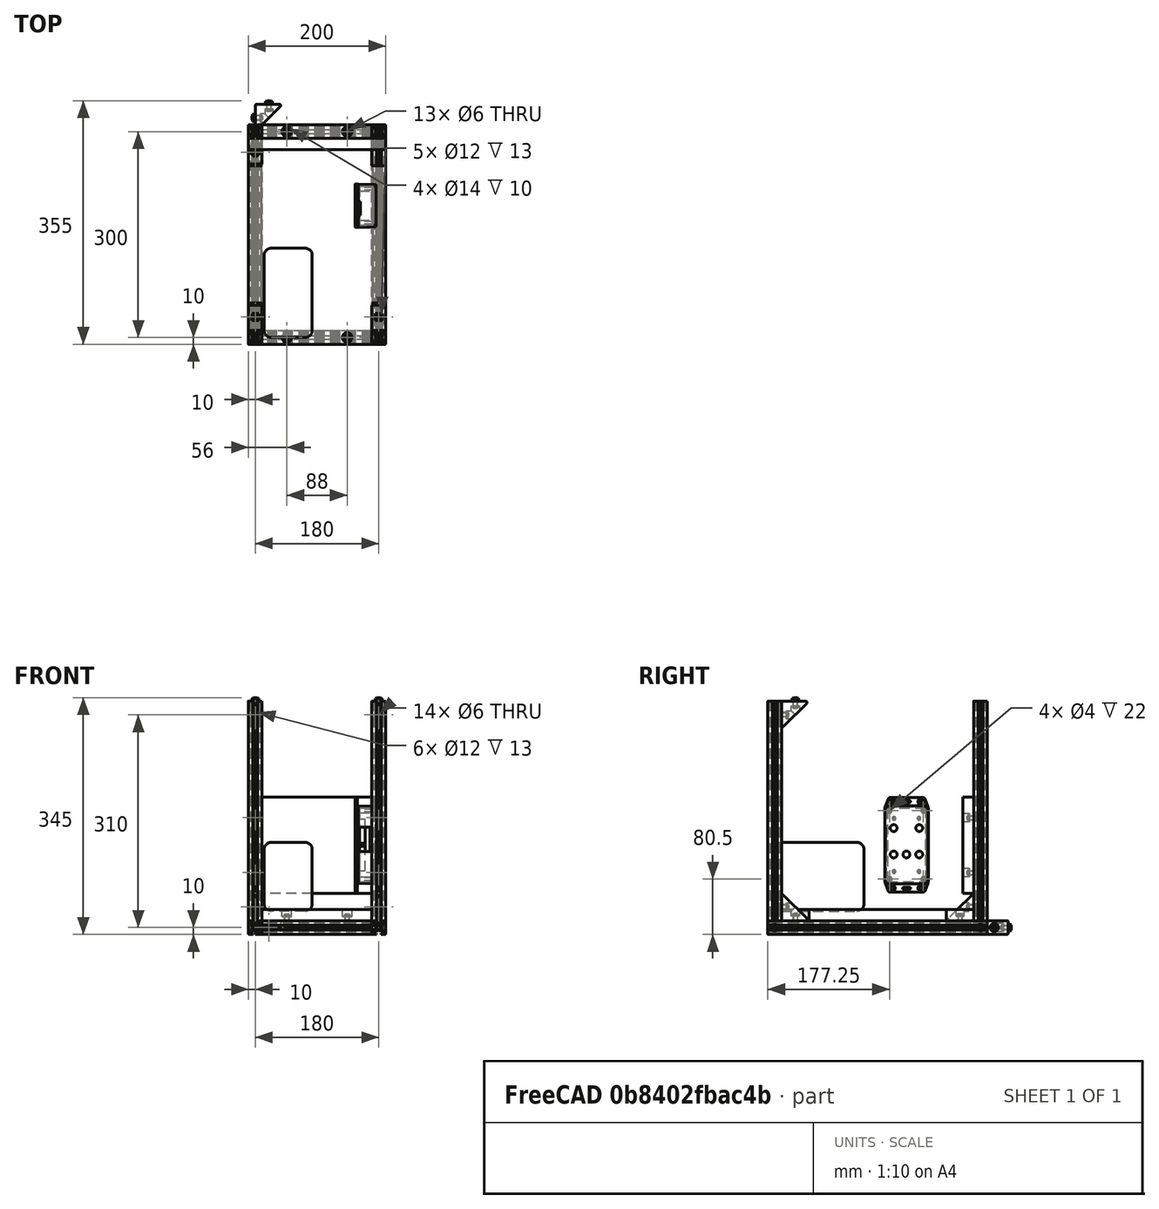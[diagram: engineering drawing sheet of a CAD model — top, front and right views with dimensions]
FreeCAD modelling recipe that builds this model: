
FCSTD DOCUMENT  (FreeCAD 0.17R9796 (Git))
Label: UPKframeNG2c
License: All rights reserved
LicenseURL: http://en.wikipedia.org/wiki/All_rights_reserved
objects: Part::Feature×55, Part::FeaturePython×20, Part::Compound×11, App::Part×6, Part::Cylinder×5, App::FeaturePython×4, Part::Box×4, Part::Cut×4, PartDesign::Body×1, PartDesign::Pocket×1, Part::Fillet×1, Part::MultiFuse×1
note: 104 computed .brp shape members not serialized (recipe doc carries the construction recipe); baked Part::Feature solids carry a one-line shape summary decoded from their .brp

FEATURE [Part::Feature] Pocket003001  label="tslot32con"
  Placement = pos=(0,10,10) rot=(1,0,0;1.5708rad)
  shape: bbox 20 x 320 x 20 mm, 150 faces (baked)
FEATURE [Part::Feature] Pocket003002  label="tslot16"
  Placement = pos=(10,0,10) rot=(0,1,0;1.5708rad)
  shape: bbox 160 x 20 x 20 mm, 94 faces (baked)
FEATURE [Part::Feature] Pocket003006  label="tslot16_001"
  Placement = pos=(10,-300,10) rot=(0,1,0;1.5708rad)
  shape: bbox 160 x 20 x 20 mm, 94 faces (baked)
FEATURE [Part::Feature] Pocket003007  label="tslot32con_001"
  Placement = pos=(180,-310,10) rot=(0,0.707107,0.707107;3.14159rad)
  shape: bbox 20 x 320 x 20 mm, 150 faces (baked)
FEATURE [Part::FeaturePython] Screw  label="M6x25-Screw"  # Fasteners workbench fastener (typed FeaturePython)
  Placement = pos=(-4,0,10) rot=(0,-1,0;1.5708rad)
  diameter = 7
  invert = false
  length = 6
  matchOuter = false
  offset = 0
  thread = false
  type = 15
FEATURE [Part::FeaturePython] Screw001  label="M6x25-Screw004"  # Fasteners workbench fastener (typed FeaturePython)
  Placement = pos=(-4,-300,10) rot=(0,-1,0;1.5708rad)
  diameter = 7
  invert = false
  length = 6
  matchOuter = false
  offset = 0
  thread = false
  type = 15
FEATURE [Part::FeaturePython] Screw002  label="M6x25-Screw005"  # Fasteners workbench fastener (typed FeaturePython)
  Placement = pos=(184,0,10) rot=(0,1,0;1.5708rad)
  diameter = 7
  invert = false
  length = 6
  matchOuter = false
  offset = 0
  thread = false
  type = 15
FEATURE [Part::FeaturePython] Screw004  label="M6x25-Screw006"  # Fasteners workbench fastener (typed FeaturePython)
  Placement = pos=(184,-300,10) rot=(0,1,0;1.5708rad)
  diameter = 7
  invert = false
  length = 6
  matchOuter = false
  offset = 0
  thread = false
  type = 15
FEATURE [App::Part] Part  label="lower_frame"
  Group = -> [Pocket003001,Pocket003002,Pocket003006,Pocket003007,Screw,Screw001,Screw002,Screw004]
  License = CC BY 3.0
  LicenseURL = http://creativecommons.org/licenses/by/3.0/
  Origin = -> PartOrigin
FEATURE [Part::Feature] Pocket003008  label="tslot32con001"
  Placement = pos=(0,10,10) rot=(1,0,0;1.5708rad)
  shape: bbox 20 x 320 x 20 mm, 150 faces (baked)
FEATURE [Part::Feature] Pocket003009  label="tslot041"
  Placement = pos=(10,0,10) rot=(0,1,0;1.5708rad)
  shape: bbox 160 x 20 x 20 mm, 94 faces (baked)
FEATURE [Part::Feature] Pocket003010  label="tslot16_002"
  Placement = pos=(10,-300,10) rot=(0,1,0;1.5708rad)
  shape: bbox 160 x 20 x 20 mm, 94 faces (baked)
FEATURE [Part::Feature] Pocket003011  label="tslot32con_002"
  Placement = pos=(180,-310,10) rot=(0,0.707107,0.707107;3.14159rad)
  shape: bbox 20 x 320 x 20 mm, 150 faces (baked)
FEATURE [Part::FeaturePython] Screw005  label="M6x25-Screw007"  # Fasteners workbench fastener (typed FeaturePython)
  Placement = pos=(-4,0,10) rot=(0,-1,0;1.5708rad)
  diameter = 7
  invert = false
  length = 6
  matchOuter = false
  offset = 0
  thread = false
  type = 15
FEATURE [Part::FeaturePython] Screw006  label="M6x25-Screw008"  # Fasteners workbench fastener (typed FeaturePython)
  Placement = pos=(-4,-300,10) rot=(0,-1,0;1.5708rad)
  diameter = 7
  invert = false
  length = 6
  matchOuter = false
  offset = 0
  thread = false
  type = 15
FEATURE [Part::FeaturePython] Screw007  label="M6x25-Screw009"  # Fasteners workbench fastener (typed FeaturePython)
  Placement = pos=(184,0,10) rot=(0,1,0;1.5708rad)
  diameter = 7
  invert = false
  length = 6
  matchOuter = false
  offset = 0
  thread = false
  type = 15
FEATURE [Part::FeaturePython] Screw008  label="M6x25-Screw010"  # Fasteners workbench fastener (typed FeaturePython)
  Placement = pos=(184,-300,10) rot=(0,1,0;1.5708rad)
  diameter = 7
  invert = false
  length = 6
  matchOuter = false
  offset = 0
  thread = false
  type = 15
FEATURE [App::Part] Part001  label="upper_frame"
  Group = -> [Pocket003008,Pocket003009,Pocket003010,Pocket003011,Screw005,Screw006,Screw007,Screw008]
  License = CC BY 3.0
  LicenseURL = http://creativecommons.org/licenses/by/3.0/
  Origin = -> PartOrigin001
  Placement = pos=(0,0,340) rot=(0,0,1;0rad)
FEATURE [Part::Feature] Fillet004001  label="Fillet005"
  shape: bbox 37.5 x 37.5 x 20 mm, 26 faces (baked)
FEATURE [Part::FeaturePython] Screw009  label="M6x12-Screw"  # Fasteners workbench fastener (typed FeaturePython)
  Placement = pos=(7,20,10) rot=(0,1,0;1.5708rad)
  diameter = 4
  invert = false
  length = 1
  matchOuter = false
  offset = 0
  thread = false
  type = 20
FEATURE [Part::Feature] Body001  label="m6nutplate"
  Placement = pos=(-1.5,15,5) rot=(0,-1,0;1.5708rad)
  shape: bbox 3 x 10 x 10 mm, 9 faces (baked)
FEATURE [App::Part] Part002  label="cornerstonescrewnut"
  License = CC BY 3.0
  LicenseURL = http://creativecommons.org/licenses/by/3.0/
  Origin = -> PartOrigin002
  Placement = pos=(10,-50,20) rot=(0,-1,0;1.5708rad)
FEATURE [Part::FeaturePython] Screw010  label="M6x12-Screw001"  # Fasteners workbench fastener (typed FeaturePython)
  Placement = pos=(20,33,10) rot=(1,0,0;1.5708rad)
  diameter = 4
  invert = false
  length = 1
  matchOuter = false
  offset = 0
  thread = false
  type = 20
FEATURE [Part::Feature] Body002  label="m6nutplate001"
  Placement = pos=(15,41.5,5) rot=(0.57735,0.57735,0.57735;4.18879rad)
  shape: bbox 10 x 3 x 10 mm, 9 faces (baked)
FEATURE [Part::Feature] Fillet004002  label="Fillet006"
  shape: bbox 37.5 x 37.5 x 20 mm, 26 faces (baked)
FEATURE [Part::FeaturePython] Screw011  label="M6x12-Screw002"  # Fasteners workbench fastener (typed FeaturePython)
  Placement = pos=(7,20,10) rot=(0,1,0;1.5708rad)
  diameter = 4
  invert = false
  length = 1
  matchOuter = false
  offset = 0
  thread = false
  type = 20
FEATURE [Part::Feature] Body003  label="m6nutplate002"
  Placement = pos=(-1.5,15,5) rot=(0,-1,0;1.5708rad)
  shape: bbox 3 x 10 x 10 mm, 9 faces (baked)
FEATURE [Part::FeaturePython] Screw012  label="M6x12-Screw003"  # Fasteners workbench fastener (typed FeaturePython)
  Placement = pos=(20,33,10) rot=(1,0,0;1.5708rad)
  diameter = 4
  invert = false
  length = 1
  matchOuter = false
  offset = 0
  thread = false
  type = 20
FEATURE [Part::Feature] Body004  label="m6nutplate003"
  Placement = pos=(15,41.5,5) rot=(0.57735,0.57735,0.57735;4.18879rad)
  shape: bbox 10 x 3 x 10 mm, 9 faces (baked)
FEATURE [App::Part] Part003  label="cornerstonescrewnut001"
  Group = -> [Body003,Screw011,Fillet004002,Screw012,Body004,PartOrigin002,Body001,Screw009,Fillet004001,Screw010,Body002,Part002]
  License = CC BY 3.0
  LicenseURL = http://creativecommons.org/licenses/by/3.0/
  Origin = -> PartOrigin003
  Placement = pos=(190,-50,20) rot=(0,-1,0;1.5708rad)
FEATURE [Part::Feature] Fillet004003  label="Fillet007"
  shape: bbox 37.5 x 37.5 x 20 mm, 26 faces (baked)
FEATURE [Part::FeaturePython] Screw013  label="M6x12-Screw004"  # Fasteners workbench fastener (typed FeaturePython)
  Placement = pos=(7,20,10) rot=(0,1,0;1.5708rad)
  diameter = 4
  invert = false
  length = 1
  matchOuter = false
  offset = 0
  thread = false
  type = 20
FEATURE [Part::Feature] Body005  label="m6nutplate004"
  Placement = pos=(-1.5,15,5) rot=(0,-1,0;1.5708rad)
  shape: bbox 3 x 10 x 10 mm, 9 faces (baked)
FEATURE [Part::FeaturePython] Screw014  label="M6x12-Screw005"  # Fasteners workbench fastener (typed FeaturePython)
  Placement = pos=(20,33,10) rot=(1,0,0;1.5708rad)
  diameter = 4
  invert = false
  length = 1
  matchOuter = false
  offset = 0
  thread = false
  type = 20
FEATURE [Part::Feature] Body006  label="m6nutplate005"
  Placement = pos=(15,41.5,5) rot=(0.57735,0.57735,0.57735;4.18879rad)
  shape: bbox 10 x 3 x 10 mm, 9 faces (baked)
FEATURE [App::Part] Part004  label="cornerstonescrewnut002"
  Group = -> [Body005,Screw013,Fillet004003,Screw014,Body006]
  License = CC BY 3.0
  LicenseURL = http://creativecommons.org/licenses/by/3.0/
  Origin = -> PartOrigin004
  Placement = pos=(-10,-50,340) rot=(0,1,0;1.5708rad)
FEATURE [Part::Feature] Fillet004004  label="Fillet008"
  shape: bbox 37.5 x 37.5 x 20 mm, 26 faces (baked)
FEATURE [Part::FeaturePython] Screw015  label="M6x12-Screw006"  # Fasteners workbench fastener (typed FeaturePython)
  Placement = pos=(7,20,10) rot=(0,1,0;1.5708rad)
  diameter = 4
  invert = false
  length = 1
  matchOuter = false
  offset = 0
  thread = false
  type = 20
FEATURE [Part::Feature] Body007  label="m6nutplate006"
  Placement = pos=(-1.5,15,5) rot=(0,-1,0;1.5708rad)
  shape: bbox 3 x 10 x 10 mm, 9 faces (baked)
FEATURE [Part::FeaturePython] Screw016  label="M6x12-Screw007"  # Fasteners workbench fastener (typed FeaturePython)
  Placement = pos=(20,33,10) rot=(1,0,0;1.5708rad)
  diameter = 4
  invert = false
  length = 1
  matchOuter = false
  offset = 0
  thread = false
  type = 20
FEATURE [Part::Feature] Body008  label="m6nutplate007"
  Placement = pos=(15,41.5,5) rot=(0.57735,0.57735,0.57735;4.18879rad)
  shape: bbox 10 x 3 x 10 mm, 9 faces (baked)
FEATURE [App::Part] Part005  label="cornerstonescrewnut003"
  Group = -> [Body007,Screw015,Fillet004004,Screw016,Body008]
  License = CC BY 3.0
  LicenseURL = http://creativecommons.org/licenses/by/3.0/
  Origin = -> PartOrigin005
  Placement = pos=(170,-50,340) rot=(0,1,0;1.5708rad)
FEATURE [Part::Feature] Body009001  label="m6nutplate010"
  Placement = pos=(-1.5,15,5) rot=(0,-1,0;1.5708rad)
  shape: bbox 3 x 10 x 10 mm, 9 faces (baked)
FEATURE [Part::Feature] Body010001  label="m6nutplate011"
  Placement = pos=(15,41.5,5) rot=(0.57735,0.57735,0.57735;4.18879rad)
  shape: bbox 10 x 3 x 10 mm, 9 faces (baked)
FEATURE [Part::Feature] Screw018001  label="M6x12-Screw010"
  Placement = pos=(20,33,10) rot=(1,0,0;1.5708rad)
  shape: bbox 10.5 x 15.3 x 10.5 mm, 15 faces (baked)
FEATURE [Part::Feature] Screw017001  label="M6x12-Screw011"
  Placement = pos=(7,20,10) rot=(0,1,0;1.5708rad)
  shape: bbox 15.3 x 10.5 x 10.5 mm, 15 faces (baked)
FEATURE [Part::Feature] Fillet004005001  label="Fillet010"
  shape: bbox 37.5 x 37.5 x 20 mm, 26 faces (baked)
FEATURE [Part::Compound] Compound
  Links = -> [Body009001,Fillet004005001,Screw017001,Body010001,Screw018001]
  Placement = pos=(10,-250,340) rot=(0.707107,0,-0.707107;3.14159rad)
FEATURE [Part::Feature] Body010002  label="m6nutplate012"
  Placement = pos=(-1.5,15,5) rot=(0,-1,0;1.5708rad)
  shape: bbox 3 x 10 x 10 mm, 9 faces (baked)
FEATURE [Part::Feature] Body010003  label="m6nutplate013"
  Placement = pos=(15,41.5,5) rot=(0.57735,0.57735,0.57735;4.18879rad)
  shape: bbox 10 x 3 x 10 mm, 9 faces (baked)
FEATURE [Part::Feature] Screw018002  label="M6x12-Screw012"
  Placement = pos=(20,33,10) rot=(1,0,0;1.5708rad)
  shape: bbox 10.5 x 15.3 x 10.5 mm, 15 faces (baked)
FEATURE [Part::Feature] Screw018003  label="M6x12-Screw013"
  Placement = pos=(7,20,10) rot=(0,1,0;1.5708rad)
  shape: bbox 15.3 x 10.5 x 10.5 mm, 15 faces (baked)
FEATURE [Part::Feature] Fillet004005002  label="Fillet011"
  shape: bbox 37.5 x 37.5 x 20 mm, 26 faces (baked)
FEATURE [Part::Compound] Compound001
  Links = -> [Body010002,Fillet004005002,Screw018003,Body010003,Screw018002]
  Placement = pos=(190,-250,340) rot=(0.707107,0,-0.707107;3.14159rad)
FEATURE [Part::Feature] Body010004  label="m6nutplate014"
  Placement = pos=(-1.5,15,5) rot=(0,-1,0;1.5708rad)
  shape: bbox 3 x 10 x 10 mm, 9 faces (baked)
FEATURE [Part::Feature] Body010005  label="m6nutplate015"
  Placement = pos=(15,41.5,5) rot=(0.57735,0.57735,0.57735;4.18879rad)
  shape: bbox 10 x 3 x 10 mm, 9 faces (baked)
FEATURE [Part::Feature] Screw018004  label="M6x12-Screw014"
  Placement = pos=(20,33,10) rot=(1,0,0;1.5708rad)
  shape: bbox 10.5 x 15.3 x 10.5 mm, 15 faces (baked)
FEATURE [Part::Feature] Screw018005  label="M6x12-Screw015"
  Placement = pos=(7,20,10) rot=(0,1,0;1.5708rad)
  shape: bbox 15.3 x 10.5 x 10.5 mm, 15 faces (baked)
FEATURE [Part::Feature] Fillet004005003  label="Fillet012"
  shape: bbox 37.5 x 37.5 x 20 mm, 26 faces (baked)
FEATURE [Part::Compound] Compound002
  Links = -> [Body010004,Fillet004005003,Screw018005,Body010005,Screw018004]
  Placement = pos=(10,-290,60) rot=(0.57735,0.57735,-0.57735;4.18879rad)
FEATURE [Part::Feature] Body010006  label="m6nutplate016"
  Placement = pos=(-1.5,15,5) rot=(0,-1,0;1.5708rad)
  shape: bbox 3 x 10 x 10 mm, 9 faces (baked)
FEATURE [Part::Feature] Body010007  label="m6nutplate017"
  Placement = pos=(15,41.5,5) rot=(0.57735,0.57735,0.57735;4.18879rad)
  shape: bbox 10 x 3 x 10 mm, 9 faces (baked)
FEATURE [Part::Feature] Screw018006  label="M6x12-Screw016"
  Placement = pos=(20,33,10) rot=(1,0,0;1.5708rad)
  shape: bbox 10.5 x 15.3 x 10.5 mm, 15 faces (baked)
FEATURE [Part::Feature] Screw018007  label="M6x12-Screw017"
  Placement = pos=(7,20,10) rot=(0,1,0;1.5708rad)
  shape: bbox 15.3 x 10.5 x 10.5 mm, 15 faces (baked)
FEATURE [Part::Feature] Fillet004005004  label="Fillet013"
  shape: bbox 37.5 x 37.5 x 20 mm, 26 faces (baked)
FEATURE [Part::Compound] Compound003
  Links = -> [Body010006,Fillet004005004,Screw018007,Body010007,Screw018006]
  Placement = pos=(190,-290,60) rot=(0.57735,0.57735,-0.57735;4.18879rad)
FEATURE [Part::Feature] Pocket001001  label="tslot32"
  Placement = pos=(0,0,20) rot=(0,0,1;0rad)
  shape: bbox 20 x 20 x 320 mm, 94 faces (baked)
FEATURE [Part::Feature] Body010008  label="m6nutplate018"
  Placement = pos=(-1.5,15,5) rot=(0,-1,0;1.5708rad)
  shape: bbox 3 x 10 x 10 mm, 9 faces (baked)
FEATURE [Part::Feature] Body010009  label="m6nutplate019"
  Placement = pos=(15,41.5,5) rot=(0.57735,0.57735,0.57735;4.18879rad)
  shape: bbox 10 x 3 x 10 mm, 9 faces (baked)
FEATURE [Part::Feature] Screw018008  label="M6x12-Screw018"
  Placement = pos=(20,33,10) rot=(1,0,0;1.5708rad)
  shape: bbox 10.5 x 15.3 x 10.5 mm, 15 faces (baked)
FEATURE [Part::Feature] Screw018009  label="M6x12-Screw019"
  Placement = pos=(7,20,10) rot=(0,1,0;1.5708rad)
  shape: bbox 15.3 x 10.5 x 10.5 mm, 15 faces (baked)
FEATURE [Part::Feature] Fillet004005005  label="Fillet014"
  shape: bbox 37.5 x 37.5 x 20 mm, 26 faces (baked)
FEATURE [Part::Compound] Compound004
  Links = -> [Body010008,Fillet004005005,Screw018009,Body010009,Screw018008]
  Placement = pos=(-10,-10,60) rot=(0.57735,-0.57735,0.57735;4.18879rad)
FEATURE [Part::Feature] Pocket003012  label="tslot32_001"
  Placement = pos=(0,-300,20) rot=(0,0,1;0rad)
  shape: bbox 20 x 20 x 320 mm, 94 faces (baked)
FEATURE [Part::Feature] Pocket003013  label="tslot32_002"
  Placement = pos=(180,0,20) rot=(0,0,1;0rad)
  shape: bbox 20 x 20 x 320 mm, 94 faces (baked)
FEATURE [Part::Feature] Pocket003014  label="tslot32_003"
  Placement = pos=(180,-300,20) rot=(0,0,1;0rad)
  shape: bbox 20 x 20 x 320 mm, 94 faces (baked)
FEATURE [PartDesign::Body] Body010027
FEATURE [Part::FeaturePython] Screw018021  label="M6x12-Screw032"  # Fasteners workbench fastener (typed FeaturePython)
  diameter = 4
  invert = false
  length = 1
  matchOuter = false
  offset = 0
  thread = false
  type = 20
FEATURE [Part::Feature] Body010028  label="m6nutplate032"
  Placement = pos=(5,-5,-8.39) rot=(0,1,0;3.14159rad)
  shape: bbox 10 x 10 x 3 mm, 9 faces (baked)
FEATURE [App::FeaturePython] circularEdgeConstraint009  # a2plus constraint (typed FeaturePython)
  Object1 = Screw
  Object2 = Body001
  SubElement1 = Edge7
  SubElement2 = Edge20
  Type = circularEdge
  directionConstraint = 1
  lockRotation = false
  offset = 0
FEATURE [Part::Compound] Compound017  label="nutplate12screw008"
  Links = -> [Screw018021,circularEdgeConstraint009,Body010028]
  Placement = pos=(10,30,6) rot=(0,0,1;0rad)
FEATURE [Part::FeaturePython] Screw018022  label="M6x12-Screw033"  # Fasteners workbench fastener (typed FeaturePython)
  diameter = 4
  invert = false
  length = 1
  matchOuter = false
  offset = 0
  thread = false
  type = 20
FEATURE [Part::Feature] Body010029  label="m6nutplate033"
  Placement = pos=(5,-5,-8.39) rot=(0,1,0;3.14159rad)
  shape: bbox 10 x 10 x 3 mm, 9 faces (baked)
FEATURE [App::FeaturePython] circularEdgeConstraint010  # a2plus constraint (typed FeaturePython)
  Object1 = Screw
  Object2 = Body001
  SubElement1 = Edge7
  SubElement2 = Edge20
  Type = circularEdge
  directionConstraint = 1
  lockRotation = false
  offset = 0
FEATURE [Part::Compound] Compound018  label="nutplate12screw009"
  Links = -> [Screw018022,circularEdgeConstraint010,Body010029]
  Placement = pos=(10,110,6) rot=(0,0,1;0rad)
FEATURE [Part::FeaturePython] Screw018023  label="M6x12-Screw034"  # Fasteners workbench fastener (typed FeaturePython)
  diameter = 4
  invert = false
  length = 1
  matchOuter = false
  offset = 0
  thread = false
  type = 20
FEATURE [Part::Feature] Body010030  label="m6nutplate034"
  Placement = pos=(5,-5,-8.39) rot=(0,1,0;3.14159rad)
  shape: bbox 10 x 10 x 3 mm, 9 faces (baked)
FEATURE [App::FeaturePython] circularEdgeConstraint011  # a2plus constraint (typed FeaturePython)
  Object1 = Screw
  Object2 = Body001
  SubElement1 = Edge7
  SubElement2 = Edge20
  Type = circularEdge
  directionConstraint = 1
  lockRotation = false
  offset = 0
FEATURE [Part::Compound] Compound019  label="nutplate12screw010"
  Links = -> [Screw018023,circularEdgeConstraint011,Body010030]
  Placement = pos=(190,110,6) rot=(0,0,1;0rad)
FEATURE [Part::FeaturePython] Screw018024  label="M6x12-Screw035"  # Fasteners workbench fastener (typed FeaturePython)
  diameter = 4
  invert = false
  length = 1
  matchOuter = false
  offset = 0
  thread = false
  type = 20
FEATURE [Part::Feature] Body010031  label="m6nutplate035"
  Placement = pos=(5,-5,-8.39) rot=(0,1,0;3.14159rad)
  shape: bbox 10 x 10 x 3 mm, 9 faces (baked)
FEATURE [App::FeaturePython] circularEdgeConstraint012  # a2plus constraint (typed FeaturePython)
  Object1 = Screw
  Object2 = Body001
  SubElement1 = Edge7
  SubElement2 = Edge20
  Type = circularEdge
  directionConstraint = 1
  lockRotation = false
  offset = 0
FEATURE [Part::Compound] Compound020  label="nutplate12screw011"
  Links = -> [Screw018024,circularEdgeConstraint012,Body010031]
  Placement = pos=(190,30,6) rot=(0,0,1;0rad)
FEATURE [Part::Compound] Compound021  label="front_plate"
  Links = -> [Body010027,Compound020,Compound019,Compound017,Compound018]
  Placement = pos=(-10,-10,60) rot=(1,0,0;1.5708rad)
FEATURE [Part::Compound] Compound016  label="bottom_plate"
  Placement = pos=(190,-310,20) rot=(0,0,1;1.5708rad)
FEATURE [PartDesign::Pocket] Pocket003019
  Length = 10
  Placement = pos=(130,-166,235) rot=(0,1,0;1.5708rad)
  Type = 0
FEATURE [Part::Box] Box003  label="MPPT"
  AttacherType = Attacher::AttachEngine3D
  Height = 100
  Length = 130
  Placement = pos=(290,128,10) rot=(0,0,1;0rad)
  Width = 70
FEATURE [Part::Fillet] Fillet007  label="MPPT               "
  Base = -> Box003
  Edges = 12 edges r=10: [Edge1,Edge2,Edge3,Edge4,Edge5,Edge6,Edge7,Edge8,Edge9,Edge10,Edge11,Edge12]
  Placement = pos=(211,-590,24) rot=(0,0,1;1.5708rad)
FEATURE [Part::Feature] Part__Feature1213  label="1591XXBF LID"
  Placement = pos=(150,-86,180) rot=(-0.57735,0.57735,0.57735;4.18879rad)
  shape: bbox 12.61 x 63.32 x 138 mm, 220 faces (baked)
FEATURE [Part::Feature] Part__Feature1212  label="1591XXB BOX"
  Placement = pos=(0,0,0) rot=(0,0.707107,0.707107;3.14159rad)
  shape: bbox 113.8 x 28.25 x 63.32 mm, 133 faces (baked)
FEATURE [Part::Cylinder] Cylinder  label="Zylinder"
  Angle = 360
  AttacherType = Attacher::AttachEngine3D
  Height = 60
  Placement = pos=(-14,48,18.6) rot=(1,0,0;1.5708rad)
  Radius = 5
FEATURE [Part::Cylinder] Cylinder001  label="Zylinder001"
  Angle = 360
  AttacherType = Attacher::AttachEngine3D
  Height = 60
  Placement = pos=(-14,48,0) rot=(1,0,0;1.5708rad)
  Radius = 5
FEATURE [Part::Cylinder] Cylinder002  label="Zylinder002"
  Angle = 360
  AttacherType = Attacher::AttachEngine3D
  Height = 60
  Placement = pos=(-14,48,-18.66) rot=(1,0,0;1.5708rad)
  Radius = 5
FEATURE [Part::Cylinder] Cylinder003  label="Zylinder003"
  Angle = 360
  AttacherType = Attacher::AttachEngine3D
  Height = 60
  Placement = pos=(24.49,48,18.6) rot=(1,0,0;1.5708rad)
  Radius = 5
FEATURE [Part::Cylinder] Cylinder004  label="Zylinder004"
  Angle = 360
  AttacherType = Attacher::AttachEngine3D
  Height = 60
  Placement = pos=(24.49,48,-18.66) rot=(1,0,0;1.5708rad)
  Radius = 5
FEATURE [Part::MultiFuse] Fusion
  Shapes = -> [Cylinder,Cylinder004,Cylinder003,Cylinder002,Cylinder001]
FEATURE [Part::Cut] Cut
  Base = -> Part__Feature1212
  Tool = -> Fusion
FEATURE [Part::Box] Box002  label="Würfel002"
  AttacherType = Attacher::AttachEngine3D
  Height = 10
  Length = 76
  Placement = pos=(-38,16,-36) rot=(0,0,1;0rad)
  Width = 12.6
FEATURE [Part::Cut] Cut001
  Base = -> Cut
  Tool = -> Box002
FEATURE [Part::Box] Box004  label="Würfel003"
  AttacherType = Attacher::AttachEngine3D
  Height = 10
  Length = 36
  Placement = pos=(-10,9,24) rot=(0,0,1;0rad)
  Width = 20
FEATURE [Part::Cut] Cut002
  Base = -> Cut001
  Tool = -> Box004
FEATURE [Part::Box] Box  label="Würfel"
  AttacherType = Attacher::AttachEngine3D
  Height = 20
  Length = 10
  Placement = pos=(49,23,-6) rot=(0,0,1;0rad)
  Width = 6
FEATURE [Part::Cut] Cut003  label="bms-cover"
  Base = -> Cut002
  Placement = pos=(176,-108,130.5) rot=(0.57735,-0.57735,0.57735;2.0944rad)
  Tool = -> Box
